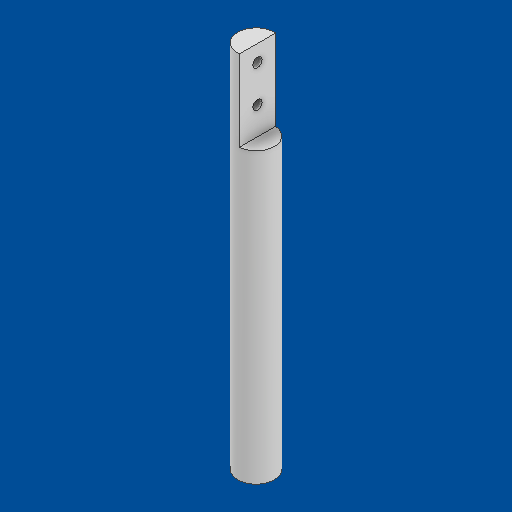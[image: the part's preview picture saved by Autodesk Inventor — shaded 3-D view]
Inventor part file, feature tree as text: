
AUTODESK INVENTOR PART (.ipt)
format: ipt  version: 2025 (Build 290162000, 162)  size: 673,792 bytes
history: native  units: mm
features: other x10, direct_edit x8, sketch x3, plane x2, split x2, hole x2, delete_face x1, extrude x1
ambient origin geometry x8: Origin, YZ Plane, XZ Plane, XY Plane, X Axis, Y Axis, Z Axis, Center Point
bodies: Solid1 (feature_tree), Solid2 (feature_tree), Solid3 (feature_tree), Solid4 (feature_tree), Solid5 (feature_tree), Solid6 (feature_tree)
feature tree (29):
  plane  "Work Plane1"
  split  "Split1"
  delete_face  "Delete Face1"
  extrude  "Extrusion1"  Depth=25.4mm TaperAngle=0.0deg
  direct_edit  "Direct Edit1"
  plane  "Work Plane3"
  split  "Split2"
  direct_edit  "Direct Edit2"
  direct_edit  "Direct Edit3"
  direct_edit  "Direct Edit4"
  direct_edit  "Direct Edit5"
  direct_edit  "Direct Edit6"
  hole  "Hole1"  [1 undecoded]
  direct_edit  "Direct Edit7"
  hole  "Hole2"  [1 undecoded]
  direct_edit  "Direct Edit8"
  sketch  "Sketch1"  dims[d0=25.0mm d1=25.4mm d2=0.0mm]
  sketch  "Sketch2"  dims[d3=-1.905mm d5=-1.27mm]
  sketch  "Sketch3"  dims[d6=99.844mm d7=-0.114mm d8=-0.019mm d9=-0.981mm d10=0.5mm d11=2.0mm d12=2.0mm d13=3.242mm d14=10.0mm d15=4.0mm d16=2.0mm d17=90.0deg d18=8.0mm d19=20.594885mm d20=1.25mm d21=3.0mm d22=4.917mm d23=40.0mm d24=4.0mm d25=2.0mm d26=90.0deg d27=40.0mm d28=20.594885mm d29=0.5mm]
  other  "13073-001-1-solid1"
  other  "21110-001-1-solid1"
  other  "Size1"
  other  "Size2"
  other  "Size3"
  other  "Size4"
  other  "Size5"
  other  "Size6"
  other  "Size7"
  other  "Size8"
note: 2 required parameter values undecoded (feature->parameter linkage not recoverable at this tier; creation-order binding heuristic only, values carry confidence <= 0.55)
